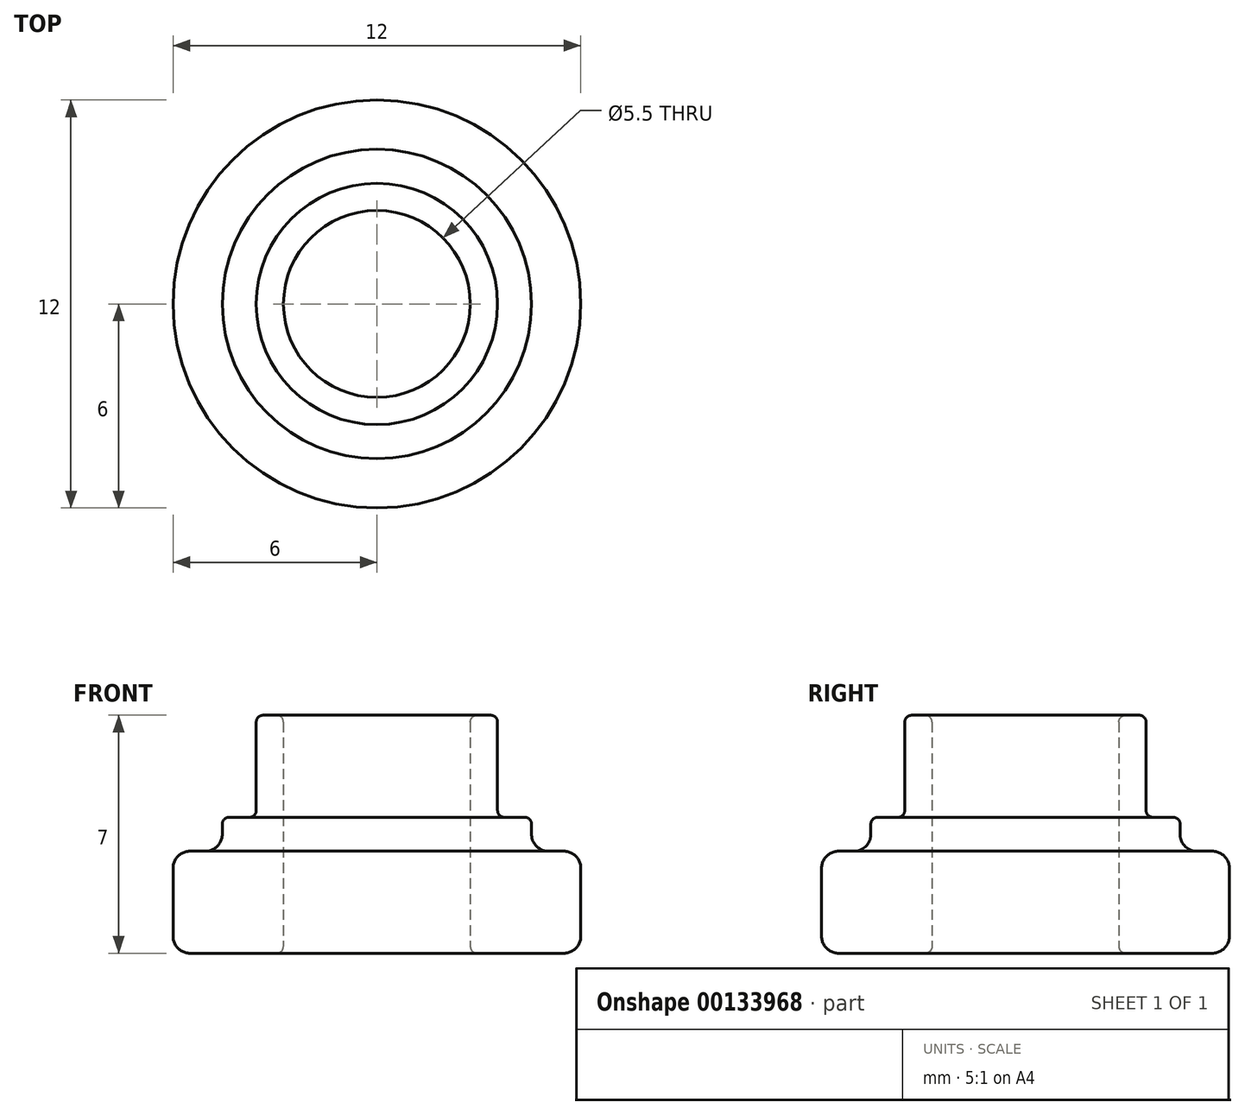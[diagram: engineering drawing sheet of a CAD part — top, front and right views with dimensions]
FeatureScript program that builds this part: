
annotation { "Feature Type Name" : "Feature", "Feature Type Description" : "" }
export const myFeature = defineFeature(function(context is Context, id is Id, definition is map)
    precondition{}
    {
        {
            var Q0;
            Q0=qCreatedBy(makeId("Front.planeOp"),FACE);
            var sketch = newSketch(context, id + "F0", { "sketchPlane" : qUnion([Q0])});
            skLineSegment(sketch, "E0", {"start": v(0, -23.61) * mm, "end": v(0, 38.56) * mm, "construction": true});
            skLineSegment(sketch, "E1", {"start": v(5.5, 0) * mm, "end": v(2.95, 0) * mm});
            skLineSegment(sketch, "E2", {"start": v(2.75, 0.2) * mm, "end": v(2.75, 6.8) * mm});
            skLineSegment(sketch, "E3", {"start": v(2.95, 7) * mm, "end": v(3.35, 7) * mm});
            skLineSegment(sketch, "E4", {"start": v(3.55, 6.8) * mm, "end": v(3.55, 4.2) * mm});
            skLineSegment(sketch, "E5", {"start": v(3.75, 4) * mm, "end": v(4.35, 4) * mm});
            skLineSegment(sketch, "E6", {"start": v(4.55, 3.8) * mm, "end": v(4.55, 3.5) * mm});
            skLineSegment(sketch, "E7", {"start": v(5.05, 3) * mm, "end": v(5.5, 3) * mm});
            skLineSegment(sketch, "E8", {"start": v(6, 2.5) * mm, "end": v(6, 0.5) * mm});
            skPoint(sketch, "E9.visualSharp", {"position": v(6, 0) * mm});
            skArc(sketch, "E9.filletArc", {"start": v(5.5, 0) * mm, "mid": v(5.85, 0.15) * mm, "end": v(6, 0.5) * mm});
            skPoint(sketch, "E10.visualSharp", {"position": v(6, 3) * mm});
            skArc(sketch, "E10.filletArc", {"start": v(6, 2.5) * mm, "mid": v(5.85, 2.85) * mm, "end": v(5.5, 3) * mm});
            skPoint(sketch, "E11.visualSharp", {"position": v(4.55, 3) * mm});
            skArc(sketch, "E11.filletArc", {"start": v(4.55, 3.5) * mm, "mid": v(4.7, 3.15) * mm, "end": v(5.05, 3) * mm});
            skPoint(sketch, "E12.visualSharp", {"position": v(2.75, 7) * mm});
            skArc(sketch, "E12.filletArc", {"start": v(2.95, 7) * mm, "mid": v(2.8, 6.94) * mm, "end": v(2.75, 6.8) * mm});
            skPoint(sketch, "E13.visualSharp", {"position": v(3.55, 7) * mm});
            skArc(sketch, "E13.filletArc", {"start": v(3.55, 6.8) * mm, "mid": v(3.5, 6.94) * mm, "end": v(3.35, 7) * mm});
            skPoint(sketch, "E14.visualSharp", {"position": v(2.75, 0) * mm});
            skArc(sketch, "E14.filletArc", {"start": v(2.75, 0.2) * mm, "mid": v(2.8, 0.06) * mm, "end": v(2.95, 0) * mm});
            skPoint(sketch, "E15.visualSharp", {"position": v(4.55, 4) * mm});
            skArc(sketch, "E15.filletArc", {"start": v(4.55, 3.8) * mm, "mid": v(4.5, 3.94) * mm, "end": v(4.35, 4) * mm});
            skPoint(sketch, "E16.visualSharp", {"position": v(3.55, 4) * mm});
            skArc(sketch, "E16.filletArc", {"start": v(3.55, 4.2) * mm, "mid": v(3.6, 4.06) * mm, "end": v(3.75, 4) * mm});
            skSolve(sketch);
        }
        {
            var Q0;
            Q0=makeQuery(id+"F0.imprint","IMPRINT",FACE,{"disambiguationData":[TD([[makeQuery(id+"F0.imprint","IMPRINT",EDGE,{"derivedFrom":sQuery(id+"F0.wireOp",EDGE,"E1")}),-1.0]])]});
            var Q1;
            Q1=sQuery(id+"F0.wireOp",EDGE,"E0");
            revolve(context, id + "F1", {"surfaceOperationType" : NewSurfaceOperationType.NEW, "entities" : qUnion([Q0]), "axis" : qUnion([Q1]), "revolveType" : RevolveType.FULL});
        }
    });
